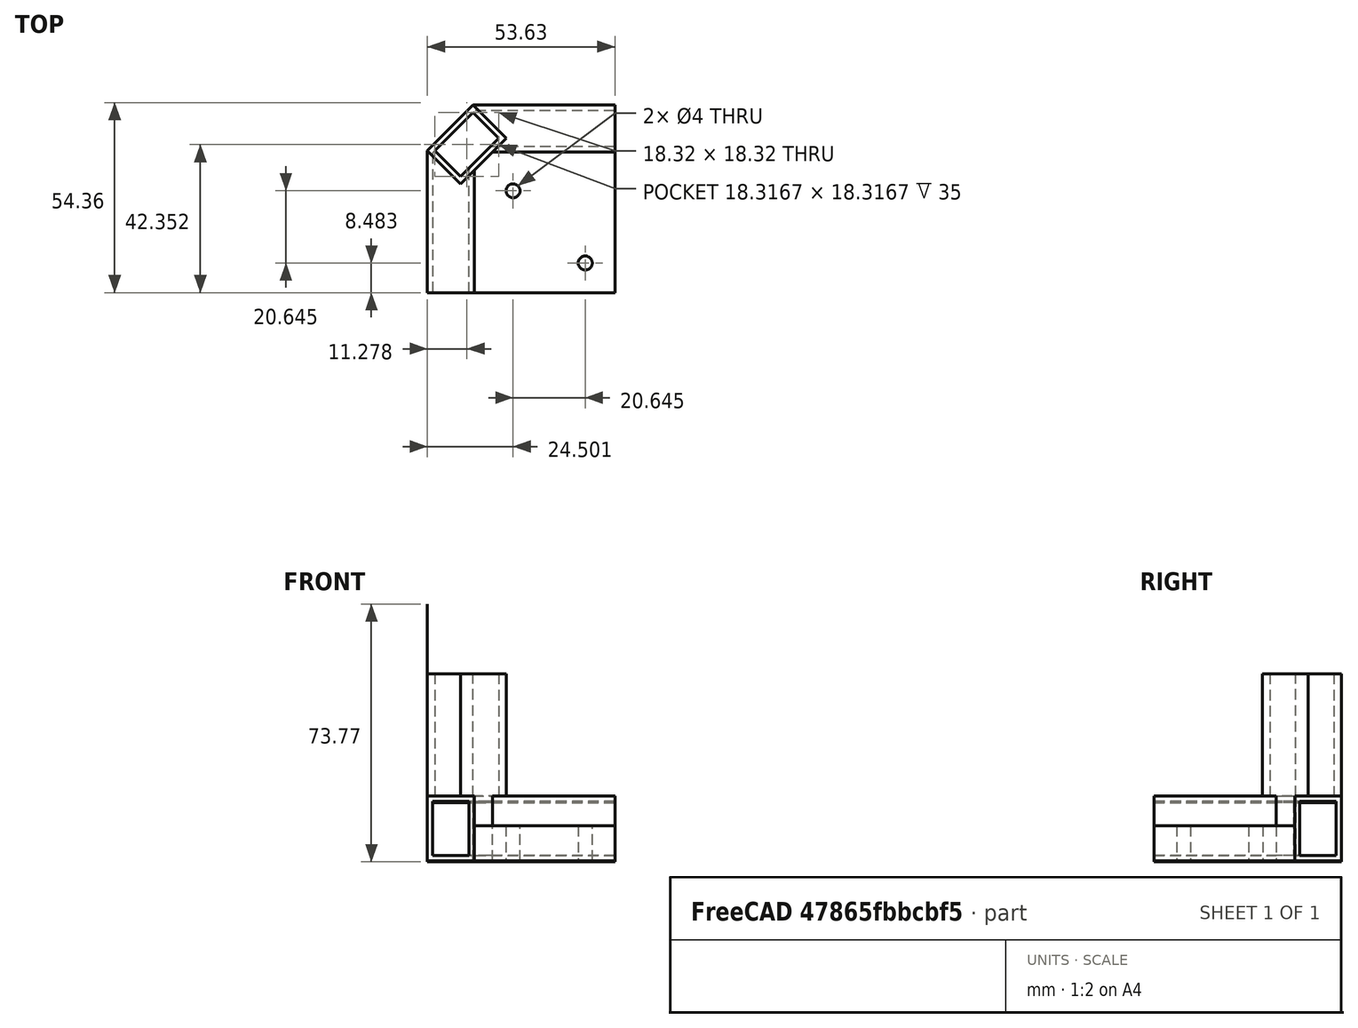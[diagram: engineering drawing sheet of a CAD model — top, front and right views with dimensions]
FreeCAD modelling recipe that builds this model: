
FCSTD DOCUMENT  (FreeCAD 1.0R39109 (Git))
Label: Smaller-Table
License: All rights reserved
LicenseURL: https://en.wikipedia.org/wiki/All_rights_reserved
objects: Sketcher::SketchObject×11, PartDesign::Pad×10, PartDesign::Pocket×4, PartDesign::Thickness×3, PartDesign::Body×3
note: 76 computed .brp shape members not serialized (recipe doc carries the construction recipe); baked Part::Feature solids carry a one-line shape summary decoded from their .brp

FEATURE [Sketcher::SketchObject] Sketch
  ArcFitTolerance = 1e-06
  AttachmentSupport = -> [XY_Plane]
  FullyConstrained = true
  MakeInternals = false
  MapMode = 5
  expr: Constraints[15] = 10.4 + 3
  sketch-geometry (9):
    g0: LineSegment StartX=-6.7 StartY=-6.38148 StartZ=0 EndX=-6.7 EndY=-46.9319 EndZ=0
    g1: LineSegment StartX=-6.7 StartY=-46.9319 StartZ=0 EndX=6.7 EndY=-46.9319 EndZ=0
    g2: LineSegment StartX=6.7 StartY=-46.9319 StartZ=0 EndX=6.7 EndY=-11.9319 EndZ=0
    g3: LineSegment StartX=6.7 StartY=-11.9319 StartZ=0 EndX=11.9319 EndY=-6.7 EndZ=0
    g4: LineSegment StartX=11.9319 StartY=-6.7 StartZ=0 EndX=46.9319 EndY=-6.7 EndZ=0
    g5: LineSegment StartX=46.9319 StartY=-6.7 StartZ=0 EndX=46.9319 EndY=6.7 EndZ=0
    g6: LineSegment StartX=46.9319 StartY=6.7 StartZ=0 EndX=6.38148 EndY=6.7 EndZ=0
    g7: LineSegment StartX=6.38148 StartY=6.7 StartZ=0 EndX=-6.7 EndY=-6.38148 EndZ=0
    g8: LineSegment [constr] StartX=11.9319 StartY=-6.7 StartZ=0 EndX=2.45671 EndY=2.77524 EndZ=0
  constraints (25):
    c: Vertical(g0)
    c: Coincident(g0,g1)
    c: Coincident(g1,g2)
    c: Vertical(g2)
    c: Coincident(g2,g3)
    c: Coincident(g3,g4)
    c: Horizontal(g4)
    c: Coincident(g4,g5)
    c: Coincident(g5,g6)
    c: Horizontal(g6)
    c: Coincident(g6,g7)
    c: Coincident(g7,g0)
    c: Symmetric(g0,g1,g-2)
    c: Symmetric(g4,g5,g-1)
    c: Angle(g2,g3) = 2.35619
    c: Distance(g1,g1) = 13.4
    c: Equal(g1,g5)
    c: DistanceY(g2,g2) = 35
    c: Equal(g2,g4)
    c: Angle(g7,g6) = 2.35619
    c: Distance(g7,g7) = 18.5
    c: Distance(g8) = 13.4
    c: Angle(g-1,g8) = 2.35619
    c: Coincident(g8,g3)
    c: PointOnObject(g8,g7)
FEATURE [PartDesign::Pad] Pad
  Direction = (0,0,1)
  Length = 18.5
  Length2 = 10
  Profile = -> Sketch
  ReferenceAxis = -> Sketch [N_Axis]
  Refine = true
  Suppressed = false
  Type = 0
FEATURE [PartDesign::Thickness] Thickness
  Base = -> Pad [Face2,Face6]
  BaseFeature = -> Pad
  Intersection = true
  Join = 0
  Mode = 0
  Refine = true
  Reversed = true
  SupportTransform = false
  Suppressed = false
  Value = 1.5
FEATURE [Sketcher::SketchObject] Sketch001
  ArcFitTolerance = 1e-06
  AttachmentSupport = -> [Thickness]
  ExternalGeometry = -> [Thickness]
  FullyConstrained = true
  MakeInternals = false
  MapMode = 5
  Placement = pos=(0,0,18.5) rot=(0,0,1;0rad)
  sketch-geometry (4):
    g0: LineSegment StartX=-6.7 StartY=-6.38148 StartZ=0 EndX=6.38148 EndY=6.7 EndZ=0
    g1: LineSegment StartX=6.38148 StartY=6.7 StartZ=0 EndX=15.8567 EndY=-2.77523 EndZ=0
    g2: LineSegment StartX=15.8567 StartY=-2.77523 StartZ=0 EndX=2.77523 EndY=-15.8567 EndZ=0
    g3: LineSegment StartX=2.77523 StartY=-15.8567 StartZ=0 EndX=-6.7 EndY=-6.38148 EndZ=0
  constraints (10):
    c: Coincident(g-3,g0)
    c: Coincident(g0,g-3)
    c: Coincident(g0,g1)
    c: Coincident(g1,g2)
    c: Coincident(g2,g3)
    c: Coincident(g3,g0)
    c: Angle(g0,g1) = 1.5708
    c: Angle(g1,g2) = 1.5708
    c: Angle(g3,g0) = 1.5708
    c: PointOnObject(g-4,g2)
FEATURE [PartDesign::Pad] Pad001
  BaseFeature = -> Thickness
  Direction = (0,0,1)
  Length = 35
  Length2 = 10
  Profile = -> Sketch001
  ReferenceAxis = -> Sketch001 [N_Axis]
  Refine = true
  Suppressed = false
  Type = 0
FEATURE [Sketcher::SketchObject] Sketch002
  ArcFitTolerance = 1e-06
  AttachmentSupport = -> [Pad001]
  ExternalGeometry = -> [Pad001]
  FullyConstrained = true
  MakeInternals = false
  MapMode = 5
  Placement = pos=(0,0,53.5) rot=(0,0,1;0rad)
  sketch-geometry (4):
    g0: LineSegment StartX=-4.58 StartY=-6.38148 StartZ=0 EndX=6.38148 EndY=4.58 EndZ=0
    g1: LineSegment StartX=6.38148 StartY=4.58 StartZ=0 EndX=13.7367 EndY=-2.77523 EndZ=0
    g2: LineSegment StartX=13.7367 StartY=-2.77523 StartZ=0 EndX=2.77523 EndY=-13.7367 EndZ=0
    g3: LineSegment StartX=2.77523 StartY=-13.7367 StartZ=0 EndX=-4.58 EndY=-6.38148 EndZ=0
  constraints (12):
    c: Coincident(g0,g1)
    c: Coincident(g1,g2)
    c: Coincident(g2,g3)
    c: Coincident(g3,g0)
    c: Horizontal(g-3,g0)
    c: Vertical(g-3,g0)
    c: Horizontal(g-4,g1)
    c: Vertical(g-4,g2)
    c: DistanceY(g-4,g2) = 2.12
    c: DistanceX(g1,g-4) = 2.12
    c: DistanceY(g0,g-3) = 2.12
    c: Distance(g-3,g0) = 2.12
FEATURE [PartDesign::Pocket] Pocket
  BaseFeature = -> Pad001
  Direction = (0,0,-1)
  Length = 35
  Length2 = 5
  Profile = -> Sketch002
  ReferenceAxis = -> Sketch002 [N_Axis]
  Refine = true
  Suppressed = false
  Type = 0
FEATURE [PartDesign::Body] Body  label="Bottom"
  AllowCompound = false
  Group = -> [Sketch,Pad,Thickness,Sketch001,Pad001,Sketch002,Pocket]
  Origin = -> Origin
  Tip = -> Pocket
FEATURE [Sketcher::SketchObject] Sketch003
  ArcFitTolerance = 1e-06
  AttachmentSupport = -> [XY_Plane001]
  FullyConstrained = true
  MakeInternals = false
  MapMode = 5
  expr: Constraints[15] = 10.4 + 3
  sketch-geometry (9):
    g0: LineSegment StartX=-6.7 StartY=-6.38148 StartZ=0 EndX=-6.7 EndY=-46.9319 EndZ=0
    g1: LineSegment StartX=-6.7 StartY=-46.9319 StartZ=0 EndX=6.7 EndY=-46.9319 EndZ=0
    g2: LineSegment StartX=6.7 StartY=-46.9319 StartZ=0 EndX=6.7 EndY=-11.9319 EndZ=0
    g3: LineSegment StartX=6.7 StartY=-11.9319 StartZ=0 EndX=11.9319 EndY=-6.7 EndZ=0
    g4: LineSegment StartX=11.9319 StartY=-6.7 StartZ=0 EndX=46.9319 EndY=-6.7 EndZ=0
    g5: LineSegment StartX=46.9319 StartY=-6.7 StartZ=0 EndX=46.9319 EndY=6.7 EndZ=0
    g6: LineSegment StartX=46.9319 StartY=6.7 StartZ=0 EndX=6.38148 EndY=6.7 EndZ=0
    g7: LineSegment StartX=6.38148 StartY=6.7 StartZ=0 EndX=-6.7 EndY=-6.38148 EndZ=0
    g8: LineSegment [constr] StartX=11.9319 StartY=-6.7 StartZ=0 EndX=2.45671 EndY=2.77524 EndZ=0
  constraints (25):
    c: Vertical(g0)
    c: Coincident(g0,g1)
    c: Coincident(g1,g2)
    c: Vertical(g2)
    c: Coincident(g2,g3)
    c: Coincident(g3,g4)
    c: Horizontal(g4)
    c: Coincident(g4,g5)
    c: Coincident(g5,g6)
    c: Horizontal(g6)
    c: Coincident(g6,g7)
    c: Coincident(g7,g0)
    c: Symmetric(g0,g1,g-2)
    c: Symmetric(g4,g5,g-1)
    c: Angle(g2,g3) = 2.35619
    c: Distance(g1,g1) = 13.4
    c: Equal(g1,g5)
    c: DistanceY(g2,g2) = 35
    c: Equal(g2,g4)
    c: Angle(g7,g6) = 2.35619
    c: Distance(g7,g7) = 18.5
    c: Distance(g8) = 13.4
    c: Angle(g-1,g8) = 2.35619
    c: Coincident(g8,g3)
    c: PointOnObject(g8,g7)
FEATURE [PartDesign::Pad] Pad002
  Direction = (0,0,1)
  Length = 18.5
  Length2 = 10
  Profile = -> Sketch003
  ReferenceAxis = -> Sketch003 [N_Axis]
  Refine = true
  Suppressed = false
  Type = 0
FEATURE [PartDesign::Thickness] Thickness001
  Base = -> Pad002 [Face2,Face6]
  BaseFeature = -> Pad002
  Intersection = true
  Join = 0
  Mode = 0
  Refine = true
  Reversed = true
  SupportTransform = false
  Suppressed = false
  Value = 1.5
FEATURE [Sketcher::SketchObject] Sketch004
  ArcFitTolerance = 1e-06
  AttachmentSupport = -> [Thickness001]
  ExternalGeometry = -> [Thickness001]
  FullyConstrained = true
  MakeInternals = false
  MapMode = 5
  Placement = pos=(0,0,18.5) rot=(0,0,1;0rad)
  sketch-geometry (4):
    g0: LineSegment StartX=-6.7 StartY=-6.38148 StartZ=0 EndX=6.38148 EndY=6.7 EndZ=0
    g1: LineSegment StartX=6.38148 StartY=6.7 StartZ=0 EndX=15.8567 EndY=-2.77523 EndZ=0
    g2: LineSegment StartX=15.8567 StartY=-2.77523 StartZ=0 EndX=2.77523 EndY=-15.8567 EndZ=0
    g3: LineSegment StartX=2.77523 StartY=-15.8567 StartZ=0 EndX=-6.7 EndY=-6.38148 EndZ=0
  constraints (10):
    c: Coincident(g-3,g0)
    c: Coincident(g0,g-3)
    c: Coincident(g0,g1)
    c: Coincident(g1,g2)
    c: Coincident(g2,g3)
    c: Coincident(g3,g0)
    c: Angle(g0,g1) = 1.5708
    c: Angle(g1,g2) = 1.5708
    c: Angle(g3,g0) = 1.5708
    c: PointOnObject(g-4,g2)
FEATURE [PartDesign::Pad] Pad003
  BaseFeature = -> Thickness001
  Direction = (0,0,1)
  Length = 35
  Length2 = 10
  Profile = -> Sketch004
  ReferenceAxis = -> Sketch004 [N_Axis]
  Refine = true
  Suppressed = false
  Type = 0
FEATURE [Sketcher::SketchObject] Sketch005
  ArcFitTolerance = 1e-06
  AttachmentSupport = -> [Pad003]
  ExternalGeometry = -> [Pad003]
  FullyConstrained = true
  MakeInternals = false
  MapMode = 5
  Placement = pos=(0,0,53.5) rot=(0,0,1;0rad)
  sketch-geometry (4):
    g0: LineSegment StartX=-4.58 StartY=-6.38148 StartZ=0 EndX=6.38148 EndY=4.58 EndZ=0
    g1: LineSegment StartX=6.38148 StartY=4.58 StartZ=0 EndX=13.7367 EndY=-2.77523 EndZ=0
    g2: LineSegment StartX=13.7367 StartY=-2.77523 StartZ=0 EndX=2.77523 EndY=-13.7367 EndZ=0
    g3: LineSegment StartX=2.77523 StartY=-13.7367 StartZ=0 EndX=-4.58 EndY=-6.38148 EndZ=0
  constraints (12):
    c: Coincident(g0,g1)
    c: Coincident(g1,g2)
    c: Coincident(g2,g3)
    c: Coincident(g3,g0)
    c: Horizontal(g-3,g0)
    c: Vertical(g-3,g0)
    c: Horizontal(g-4,g1)
    c: Vertical(g-4,g2)
    c: DistanceY(g-4,g2) = 2.12
    c: DistanceX(g1,g-4) = 2.12
    c: DistanceY(g0,g-3) = 2.12
    c: Distance(g-3,g0) = 2.12
FEATURE [PartDesign::Pocket] Pocket001
  BaseFeature = -> Pad003
  Direction = (0,0,-1)
  Length = 35
  Length2 = 5
  Profile = -> Sketch005
  ReferenceAxis = -> Sketch005 [N_Axis]
  Refine = true
  Suppressed = false
  Type = 0
FEATURE [Sketcher::SketchObject] Sketch006
  ArcFitTolerance = 1e-06
  AttachmentSupport = -> [Pocket001]
  ExternalGeometry = -> [Pocket001]
  FullyConstrained = true
  MakeInternals = false
  MapMode = 5
  Placement = pos=(0,0,0) rot=(1,0,0;3.14159rad)
  sketch-geometry (9):
    g0: LineSegment StartX=6.7 StartY=46.9319 StartZ=0 EndX=6.7 EndY=11.9319 EndZ=0
    g1: LineSegment StartX=6.7 StartY=11.9319 StartZ=0 EndX=11.9319 EndY=6.7 EndZ=0
    g2: LineSegment StartX=11.9319 StartY=6.7 StartZ=0 EndX=46.9319 EndY=6.7 EndZ=0
    g3: LineSegment StartX=46.9319 StartY=6.7 StartZ=0 EndX=46.9319 EndY=46.9319 EndZ=0
    g4: LineSegment StartX=46.9319 StartY=46.9319 StartZ=0 EndX=6.7 EndY=46.9319 EndZ=0
    g5: Circle CenterX=17.8012 CenterY=17.8012 CenterZ=0 NormalX=0 NormalY=0 NormalZ=1 AngleXU=0 Radius=2
    g6: Circle CenterX=38.4467 CenterY=38.4467 CenterZ=0 NormalX=0 NormalY=0 NormalZ=1 AngleXU=0 Radius=2
    g7: GeomPoint X=9.31597 Y=9.31597 Z=0
    g8: LineSegment [constr] StartX=9.31597 StartY=9.31597 StartZ=0 EndX=46.9319 EndY=46.9319 EndZ=0
  constraints (20):
    c: Coincident(g-3,g0)
    c: Coincident(g0,g-4)
    c: Coincident(g0,g1)
    c: Coincident(g1,g-5)
    c: Coincident(g1,g2)
    c: Coincident(g2,g-5)
    c: Coincident(g2,g3)
    c: Vertical(g3)
    c: Coincident(g3,g4)
    c: Coincident(g4,g0)
    c: Horizontal(g4)
    c: Equal(g6,g5)
    c: Diameter(g6) = 4
    c: Symmetric(g0,g1,g7)
    c: Coincident(g8,g7)
    c: Coincident(g8,g3)
    c: PointOnObject(g5,g8)
    c: PointOnObject(g6,g8)
    c: Distance(g7,g5) = 12
    c: Distance(g6,g3) = 12
FEATURE [PartDesign::Pad] Pad004
  BaseFeature = -> Pocket001
  Direction = (0,0,-1)
  Length = 10
  Length2 = 10
  Profile = -> Sketch006
  ReferenceAxis = -> Sketch006 [N_Axis]
  Refine = true
  Reversed = true
  Suppressed = false
  Type = 0
FEATURE [PartDesign::Body] Body001  label="Top"
  AllowCompound = false
  Group = -> [Sketch003,Pad002,Thickness001,Sketch004,Pad003,Sketch005,Pocket001,Sketch006,Pad004]
  Origin = -> Origin001
  Tip = -> Pad004
FEATURE [Sketcher::SketchObject] Sketch007
  ArcFitTolerance = 1e-06
  AttachmentSupport = -> [XY_Plane002]
  FullyConstrained = true
  MakeInternals = false
  MapMode = 5
  expr: Constraints[15] = 10.4 + 3
  sketch-geometry (9):
    g0: LineSegment StartX=-6.7 StartY=-6.38148 StartZ=0 EndX=-6.7 EndY=-46.9319 EndZ=0
    g1: LineSegment StartX=-6.7 StartY=-46.9319 StartZ=0 EndX=6.7 EndY=-46.9319 EndZ=0
    g2: LineSegment StartX=6.7 StartY=-46.9319 StartZ=0 EndX=6.7 EndY=-11.9319 EndZ=0
    g3: LineSegment StartX=6.7 StartY=-11.9319 StartZ=0 EndX=11.9319 EndY=-6.7 EndZ=0
    g4: LineSegment StartX=11.9319 StartY=-6.7 StartZ=0 EndX=46.9319 EndY=-6.7 EndZ=0
    g5: LineSegment StartX=46.9319 StartY=-6.7 StartZ=0 EndX=46.9319 EndY=6.7 EndZ=0
    g6: LineSegment StartX=46.9319 StartY=6.7 StartZ=0 EndX=6.38148 EndY=6.7 EndZ=0
    g7: LineSegment StartX=6.38148 StartY=6.7 StartZ=0 EndX=-6.7 EndY=-6.38148 EndZ=0
    g8: LineSegment [constr] StartX=11.9319 StartY=-6.7 StartZ=0 EndX=2.45671 EndY=2.77524 EndZ=0
  constraints (25):
    c: Vertical(g0)
    c: Coincident(g0,g1)
    c: Coincident(g1,g2)
    c: Vertical(g2)
    c: Coincident(g2,g3)
    c: Coincident(g3,g4)
    c: Horizontal(g4)
    c: Coincident(g4,g5)
    c: Coincident(g5,g6)
    c: Horizontal(g6)
    c: Coincident(g6,g7)
    c: Coincident(g7,g0)
    c: Symmetric(g0,g1,g-2)
    c: Symmetric(g4,g5,g-1)
    c: Angle(g2,g3) = 2.35619
    c: Distance(g1,g1) = 13.4
    c: Equal(g1,g5)
    c: DistanceY(g2,g2) = 35
    c: Equal(g2,g4)
    c: Angle(g7,g6) = 2.35619
    c: Distance(g7,g7) = 18.5
    c: Distance(g8) = 13.4
    c: Angle(g-1,g8) = 2.35619
    c: Coincident(g8,g3)
    c: PointOnObject(g8,g7)
FEATURE [PartDesign::Pad] Pad005
  Direction = (0,0,1)
  Length = 18.5
  Length2 = 10
  Profile = -> Sketch007
  ReferenceAxis = -> Sketch007 [N_Axis]
  Refine = true
  Suppressed = false
  Type = 0
FEATURE [PartDesign::Thickness] Thickness002
  Base = -> Pad005 [Face2,Face6]
  BaseFeature = -> Pad005
  Intersection = true
  Join = 0
  Mode = 0
  Refine = true
  Reversed = true
  SupportTransform = false
  Suppressed = false
  Value = 1.5
FEATURE [Sketcher::SketchObject] Sketch008
  ArcFitTolerance = 1e-06
  AttachmentSupport = -> [Thickness002]
  ExternalGeometry = -> [Thickness002]
  FullyConstrained = true
  MakeInternals = false
  MapMode = 5
  Placement = pos=(0,0,18.5) rot=(0,0,1;0rad)
  sketch-geometry (4):
    g0: LineSegment StartX=-6.7 StartY=-6.38148 StartZ=0 EndX=6.38148 EndY=6.7 EndZ=0
    g1: LineSegment StartX=6.38148 StartY=6.7 StartZ=0 EndX=15.8567 EndY=-2.77523 EndZ=0
    g2: LineSegment StartX=15.8567 StartY=-2.77523 StartZ=0 EndX=2.77523 EndY=-15.8567 EndZ=0
    g3: LineSegment StartX=2.77523 StartY=-15.8567 StartZ=0 EndX=-6.7 EndY=-6.38148 EndZ=0
  constraints (10):
    c: Coincident(g-3,g0)
    c: Coincident(g0,g-3)
    c: Coincident(g0,g1)
    c: Coincident(g1,g2)
    c: Coincident(g2,g3)
    c: Coincident(g3,g0)
    c: Angle(g0,g1) = 1.5708
    c: Angle(g1,g2) = 1.5708
    c: Angle(g3,g0) = 1.5708
    c: PointOnObject(g-4,g2)
FEATURE [PartDesign::Pad] Pad006
  BaseFeature = -> Thickness002
  Direction = (0,0,1)
  Length = 35
  Length2 = 10
  Profile = -> Sketch008
  ReferenceAxis = -> Sketch008 [N_Axis]
  Refine = true
  Suppressed = false
  Type = 0
FEATURE [Sketcher::SketchObject] Sketch009
  ArcFitTolerance = 1e-06
  AttachmentSupport = -> [Pad006]
  ExternalGeometry = -> [Pad006]
  FullyConstrained = true
  MakeInternals = false
  MapMode = 5
  Placement = pos=(0,0,53.5) rot=(0,0,1;0rad)
  sketch-geometry (4):
    g0: LineSegment StartX=-4.58 StartY=-6.38148 StartZ=0 EndX=6.38148 EndY=4.58 EndZ=0
    g1: LineSegment StartX=6.38148 StartY=4.58 StartZ=0 EndX=13.7367 EndY=-2.77523 EndZ=0
    g2: LineSegment StartX=13.7367 StartY=-2.77523 StartZ=0 EndX=2.77523 EndY=-13.7367 EndZ=0
    g3: LineSegment StartX=2.77523 StartY=-13.7367 StartZ=0 EndX=-4.58 EndY=-6.38148 EndZ=0
  constraints (12):
    c: Coincident(g0,g1)
    c: Coincident(g1,g2)
    c: Coincident(g2,g3)
    c: Coincident(g3,g0)
    c: Horizontal(g-3,g0)
    c: Vertical(g-3,g0)
    c: Horizontal(g-4,g1)
    c: Vertical(g-4,g2)
    c: DistanceY(g-4,g2) = 2.12
    c: DistanceX(g1,g-4) = 2.12
    c: DistanceY(g0,g-3) = 2.12
    c: Distance(g-3,g0) = 2.12
FEATURE [PartDesign::Pocket] Pocket002
  BaseFeature = -> Pad006
  Direction = (0,0,-1)
  Length = 35
  Length2 = 5
  Profile = -> Sketch009
  ReferenceAxis = -> Sketch009 [N_Axis]
  Refine = true
  Suppressed = false
  Type = 0
FEATURE [Sketcher::SketchObject] Sketch010
  ArcFitTolerance = 1e-06
  AttachmentSupport = -> [Pocket002]
  ExternalGeometry = -> [Pocket002]
  FullyConstrained = true
  MakeInternals = false
  MapMode = 5
  Placement = pos=(0,0,0) rot=(1,0,0;3.14159rad)
  sketch-geometry (9):
    g0: LineSegment StartX=6.7 StartY=46.9319 StartZ=0 EndX=6.7 EndY=11.9319 EndZ=0
    g1: LineSegment StartX=6.7 StartY=11.9319 StartZ=0 EndX=11.9319 EndY=6.7 EndZ=0
    g2: LineSegment StartX=11.9319 StartY=6.7 StartZ=0 EndX=46.9319 EndY=6.7 EndZ=0
    g3: LineSegment StartX=46.9319 StartY=6.7 StartZ=0 EndX=46.9319 EndY=46.9319 EndZ=0
    g4: LineSegment StartX=46.9319 StartY=46.9319 StartZ=0 EndX=6.7 EndY=46.9319 EndZ=0
    g5: Circle CenterX=17.8012 CenterY=17.8012 CenterZ=0 NormalX=0 NormalY=0 NormalZ=1 AngleXU=0 Radius=2
    g6: Circle CenterX=38.4467 CenterY=38.4467 CenterZ=0 NormalX=0 NormalY=0 NormalZ=1 AngleXU=0 Radius=2
    g7: GeomPoint X=9.31597 Y=9.31597 Z=0
    g8: LineSegment [constr] StartX=9.31597 StartY=9.31597 StartZ=0 EndX=46.9319 EndY=46.9319 EndZ=0
  constraints (20):
    c: Coincident(g-3,g0)
    c: Coincident(g0,g-4)
    c: Coincident(g0,g1)
    c: Coincident(g1,g-5)
    c: Coincident(g1,g2)
    c: Coincident(g2,g-5)
    c: Coincident(g2,g3)
    c: Vertical(g3)
    c: Coincident(g3,g4)
    c: Coincident(g4,g0)
    c: Horizontal(g4)
    c: Equal(g6,g5)
    c: Diameter(g6) = 4
    c: Symmetric(g0,g1,g7)
    c: Coincident(g8,g7)
    c: Coincident(g8,g3)
    c: PointOnObject(g5,g8)
    c: PointOnObject(g6,g8)
    c: Distance(g7,g5) = 12
    c: Distance(g6,g3) = 12
FEATURE [PartDesign::Pad] Pad007
  BaseFeature = -> Pocket002
  Direction = (0,0,-1)
  Length = 10
  Length2 = 10
  Profile = -> Sketch010
  ReferenceAxis = -> Sketch010 [N_Axis]
  Refine = true
  Reversed = true
  Suppressed = false
  Type = 0
FEATURE [PartDesign::Pocket] Pocket003
  BaseFeature = -> Pad007
  Direction = (0,0,-1)
  Length = 5
  Length2 = 5
  Profile = -> Pad007 [Face10]
  Refine = true
  Suppressed = false
  Type = 1
FEATURE [PartDesign::Pad] Pad008
  BaseFeature = -> Pocket003
  Direction = (0,0,-1)
  Length = 0.3
  Length2 = 10
  Profile = -> Pocket003 [Face8]
  Refine = true
  Suppressed = false
  Type = 0
FEATURE [PartDesign::Pad] Pad009
  BaseFeature = -> Pad008
  Direction = (0,0,-1)
  Length = 0.3
  Length2 = 10
  Profile = -> Pad008 [Face3]
  Refine = true
  Suppressed = false
  Type = 0
FEATURE [PartDesign::Body] Body002  label="Top001"
  AllowCompound = false
  Group = -> [Sketch007,Pad005,Thickness002,Sketch008,Pad006,Sketch009,Pocket002,Sketch010,Pad007,Pocket003,Pad008,Pad009]
  Origin = -> Origin002
  Tip = -> Pad009
